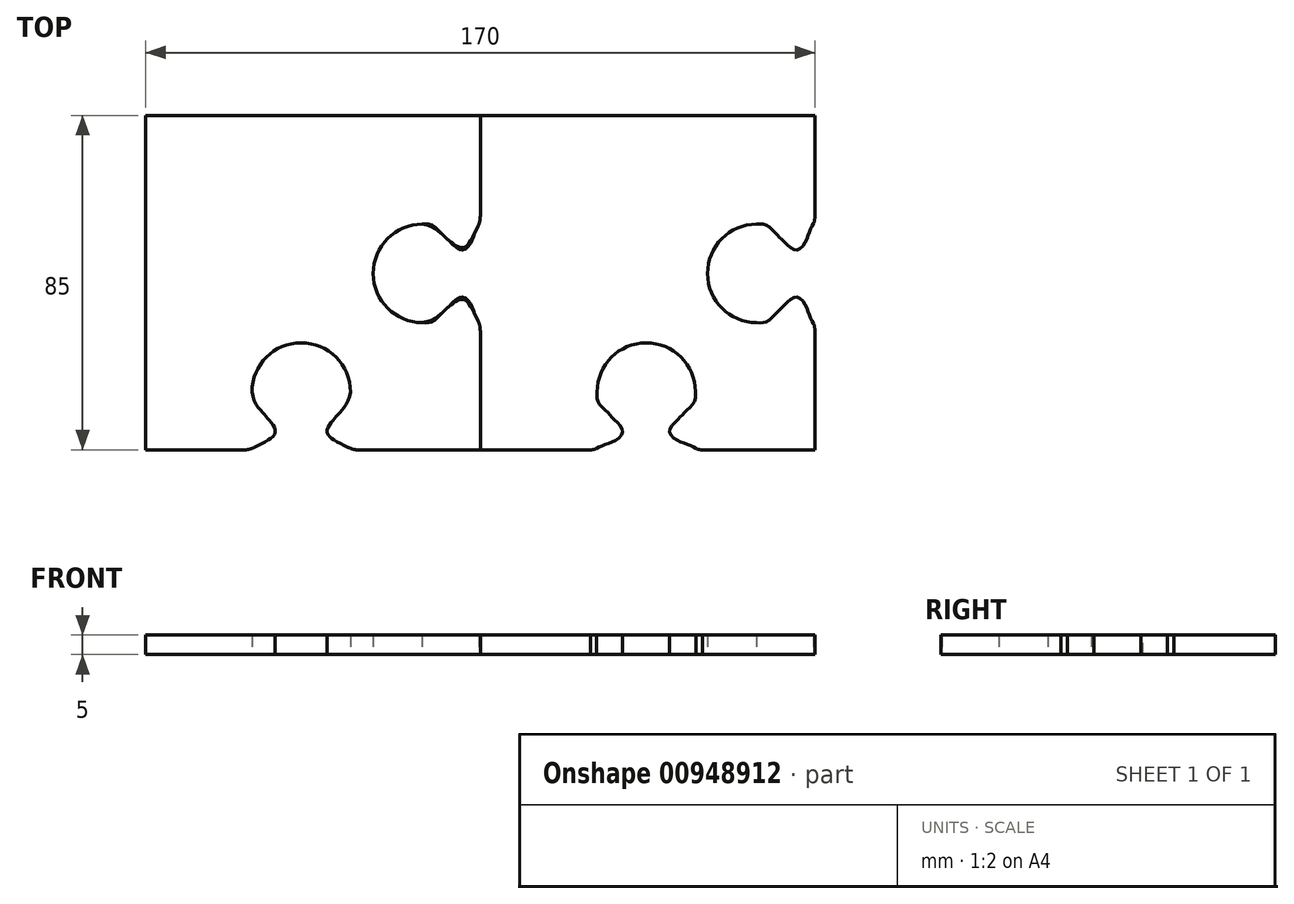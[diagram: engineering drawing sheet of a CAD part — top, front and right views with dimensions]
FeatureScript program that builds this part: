
annotation { "Feature Type Name" : "Feature", "Feature Type Description" : "" }
export const myFeature = defineFeature(function(context is Context, id is Id, definition is map)
    precondition{}
    {
        {
            var Q0;
            Q0=qCreatedBy(makeId("Top.planeOp"),FACE);
            var sketch = newSketch(context, id + "F0", { "sketchPlane" : qUnion([Q0])});
            skLineSegment(sketch, "E0.bottom", {"start": v(40, 40) * mm, "end": v(-40, 40) * mm, "construction": true});
            skLineSegment(sketch, "E0.top", {"start": v(40, -40) * mm, "end": v(-40, -40) * mm, "construction": true});
            skLineSegment(sketch, "E0.left", {"start": v(40, 40) * mm, "end": v(40, -40) * mm, "construction": true});
            skLineSegment(sketch, "E0.right", {"start": v(-40, 40) * mm, "end": v(-40, -40) * mm, "construction": true});
            skPoint(sketch, "E0.middle", {"position": v(0, 0) * mm});
            skLineSegment(sketch, "E1", {"start": v(-127.5, 127.75) * mm, "end": v(127.5, -127.75) * mm});
            skLineSegment(sketch, "E2", {"start": v(-127.5, -127.75) * mm, "end": v(127.5, 127.75) * mm});
            skSolve(sketch);
        }
        {
            var Q0;
            Q0=qCreatedBy(makeId("Top.planeOp"),FACE);
            var sketch = newSketch(context, id + "F1", { "sketchPlane" : qUnion([Q0])});
            skLineSegment(sketch, "E3", {"start": v(-127.16, 127.9) * mm, "end": v(-42.16, 127.9) * mm});
            skLineSegment(sketch, "E4", {"start": v(-42.16, 127.9) * mm, "end": v(-42.16, 102.3) * mm});
            skLineSegment(sketch, "E5", {"start": v(-42.16, 42.9) * mm, "end": v(-73.06, 42.9) * mm});
            skLineSegment(sketch, "E6", {"start": v(-127.16, 42.9) * mm, "end": v(-127.16, 127.9) * mm});
            skArc(sketch, "E7", {"start": v(-75.16, 57.66) * mm, "mid": v(-87.66, 70.1) * mm, "end": v(-100.16, 57.66) * mm});
            skFitSpline(sketch, "E8", {"points": [v(-100.8, 42.9) * mm, v(-95.44, 45.77) * mm, v(-94.25, 47.68) * mm, v(-95.69, 50.4) * mm, v(-97.5, 52.44) * mm, v(-100.16, 57.66) * mm], "startDerivative": vector(25.78, 13.8) * mm, "endDerivative": vector(-3.06, 30.92) * mm});
            skLineSegment(sketch, "E9", {"start": v(-87.66, 57.6) * mm, "end": v(-87.66, 42.9) * mm, "construction": true});
            skFitSpline(sketch, "E10.MirrorCS", {"points": [v(-74.52, 42.9) * mm, v(-79.89, 45.77) * mm, v(-81.08, 47.68) * mm, v(-79.64, 50.4) * mm, v(-77.83, 52.44) * mm, v(-75.16, 57.66) * mm], "startDerivative": vector(-25.78, 13.8) * mm, "endDerivative": vector(3.06, 30.92) * mm});
            skLineSegment(sketch, "E11.trimOffspring", {"start": v(-102.26, 42.9) * mm, "end": v(-127.16, 42.9) * mm});
            skArc(sketch, "E12", {"start": v(-56.91, 100.25) * mm, "mid": v(-69.37, 87.75) * mm, "end": v(-56.91, 75.25) * mm});
            skFitSpline(sketch, "E13", {"points": [v(-42.16, 74.6) * mm, v(-45.03, 79.97) * mm, v(-46.94, 81.17) * mm, v(-49.66, 79.72) * mm, v(-51.7, 77.92) * mm, v(-56.91, 75.25) * mm], "startDerivative": vector(-13.8, 25.78) * mm, "endDerivative": vector(-30.92, -3.06) * mm});
            skFitSpline(sketch, "E14.MirrorCS", {"points": [v(-42.16, 100.85) * mm, v(-45.03, 95.48) * mm, v(-46.94, 94.28) * mm, v(-49.66, 95.73) * mm, v(-51.7, 97.53) * mm, v(-56.91, 100.25) * mm], "startDerivative": vector(-13.8, -25.78) * mm, "endDerivative": vector(-30.92, 3.06) * mm});
            skLineSegment(sketch, "E15.trimOffspring", {"start": v(-42.16, 73.15) * mm, "end": v(-42.16, 42.9) * mm});
            skArc(sketch, "E16.filletArc", {"start": v(-42.16, 73.15) * mm, "mid": v(-42.32, 74.53) * mm, "end": v(-42.8, 75.83) * mm});
            skArc(sketch, "E17.filletArc", {"start": v(-42.8, 99.62) * mm, "mid": v(-42.32, 100.92) * mm, "end": v(-42.16, 102.3) * mm});
            skArc(sketch, "E18.filletArc", {"start": v(-75.75, 43.54) * mm, "mid": v(-74.44, 43.07) * mm, "end": v(-73.06, 42.9) * mm});
            skArc(sketch, "E19.filletArc", {"start": v(-102.26, 42.9) * mm, "mid": v(-100.88, 43.07) * mm, "end": v(-99.58, 43.54) * mm});
            skSolve(sketch);
        }
        {
            var Q0;
            Q0 = qSketchRegion(id + "F1", true);
            extrude(context, id + "F2", {"entities" : qUnion([Q0]), "depth" : 5 * mm, "offsetDistance" : 25 * mm});
        }
        {
            var Q0;
            Q0=qCreatedBy(makeId("Top.planeOp"),FACE);
            var sketch = newSketch(context, id + "F3", { "sketchPlane" : qUnion([Q0])});
            skLineSegment(sketch, "E20.0", {"start": v(-42.16, 127.9) * mm, "end": v(-42.16, 102.3) * mm});
            skArc(sketch, "E20.1", {"start": v(-42.8, 99.62) * mm, "mid": v(-42.32, 100.92) * mm, "end": v(-42.16, 102.3) * mm});
            skFitSpline(sketch, "E20.2", {"points": [v(-42.16, 100.85) * mm, v(-43.32, 98.68) * mm, v(-44.59, 95.51) * mm, v(-46.9, 93.69) * mm, v(-49.84, 95.8) * mm, v(-51.74, 97.58) * mm, v(-54.36, 100) * mm, v(-56.91, 100.25) * mm]});
            skArc(sketch, "E20.3", {"start": v(-56.91, 100.25) * mm, "mid": v(-69.37, 87.75) * mm, "end": v(-56.91, 75.25) * mm});
            skFitSpline(sketch, "E20.4", {"points": [v(-42.16, 74.6) * mm, v(-43.32, 76.77) * mm, v(-44.59, 79.94) * mm, v(-46.9, 81.76) * mm, v(-49.84, 79.66) * mm, v(-51.73, 77.86) * mm, v(-54.37, 75.5) * mm, v(-56.91, 75.25) * mm]});
            skArc(sketch, "E20.5", {"start": v(-42.16, 73.15) * mm, "mid": v(-42.32, 74.53) * mm, "end": v(-42.8, 75.83) * mm});
            skLineSegment(sketch, "E20.6", {"start": v(-42.16, 73.15) * mm, "end": v(-42.16, 42.9) * mm});
            skLineSegment(sketch, "E21", {"start": v(-42.16, 127.9) * mm, "end": v(42.84, 127.9) * mm});
            skLineSegment(sketch, "E22", {"start": v(42.84, 127.9) * mm, "end": v(42.84, 102.06) * mm});
            skLineSegment(sketch, "E23", {"start": v(42.84, 42.9) * mm, "end": v(14.31, 42.9) * mm});
            skArc(sketch, "E24.1", {"start": v(42.23, 99.81) * mm, "mid": v(42.67, 100.9) * mm, "end": v(42.84, 102.06) * mm});
            skFitSpline(sketch, "E24.2", {"points": [v(42.76, 100.85) * mm, v(41.6, 98.68) * mm, v(40.34, 95.51) * mm, v(38.02, 93.69) * mm, v(35.09, 95.8) * mm, v(33.19, 97.58) * mm, v(30.56, 100) * mm, v(28.01, 100.25) * mm]});
            skArc(sketch, "E24.3", {"start": v(28.01, 100.25) * mm, "mid": v(15.56, 87.75) * mm, "end": v(28.01, 75.25) * mm});
            skFitSpline(sketch, "E24.4", {"points": [v(42.76, 74.6) * mm, v(41.6, 76.77) * mm, v(40.34, 79.94) * mm, v(38.02, 81.76) * mm, v(35.09, 79.66) * mm, v(33.2, 77.86) * mm, v(30.56, 75.5) * mm, v(28.01, 75.25) * mm]});
            skArc(sketch, "E24.5", {"start": v(42.84, 73.39) * mm, "mid": v(42.67, 74.55) * mm, "end": v(42.23, 75.64) * mm});
            skArc(sketch, "E25.1", {"start": v(12.06, 43.49) * mm, "mid": v(13.15, 43.07) * mm, "end": v(14.31, 42.9) * mm});
            skFitSpline(sketch, "E25.2", {"points": [v(13.1, 42.95) * mm, v(10.93, 44.11) * mm, v(7.76, 45.38) * mm, v(5.94, 47.7) * mm, v(8.05, 50.63) * mm, v(9.83, 52.53) * mm, v(12.25, 55.15) * mm, v(12.5, 57.7) * mm]});
            skArc(sketch, "E25.3", {"start": v(12.5, 57.7) * mm, "mid": v(-0.02, 70.1) * mm, "end": v(-12.5, 57.66) * mm});
            skFitSpline(sketch, "E25.4", {"points": [v(-13.14, 42.9) * mm, v(-10.98, 44.07) * mm, v(-7.81, 45.33) * mm, v(-5.99, 47.65) * mm, v(-8.1, 50.59) * mm, v(-9.89, 52.48) * mm, v(-12.25, 55.11) * mm, v(-12.5, 57.66) * mm]});
            skArc(sketch, "E25.5", {"start": v(-14.15, 42.9) * mm, "mid": v(-13.1, 43.07) * mm, "end": v(-12.11, 43.44) * mm});
            skLineSegment(sketch, "E26.trimOffspring", {"start": v(-14.15, 42.9) * mm, "end": v(-42.16, 42.9) * mm});
            skLineSegment(sketch, "E27.trimOffspring", {"start": v(42.84, 73.39) * mm, "end": v(42.84, 42.9) * mm});
            skSolve(sketch);
        }
        {
            var Q0;
            Q0=makeQuery(id+"F3.imprint","IMPRINT",FACE,{"disambiguationData":[TD([[makeQuery(id+"F3.imprint","IMPRINT",EDGE,{"derivedFrom":sQuery(id+"F3.wireOp",EDGE,"E20.0")}),1.0]])]});
            extrude(context, id + "F4", {"entities" : qUnion([Q0]), "depth" : 5 * mm, "offsetDistance" : 25 * mm});
        }
    });
